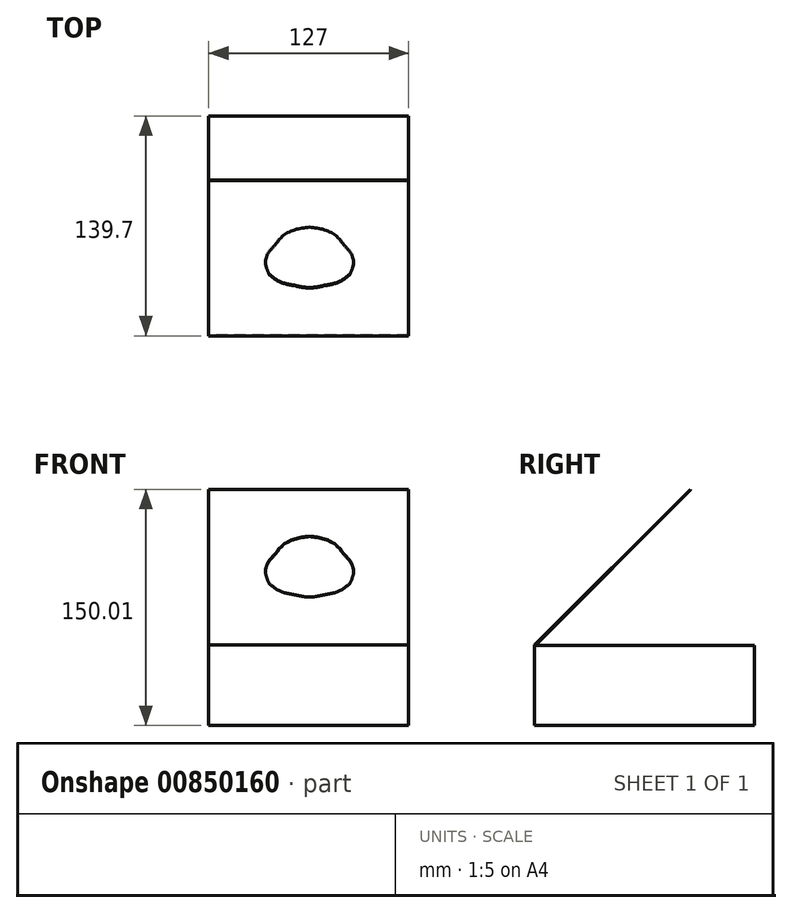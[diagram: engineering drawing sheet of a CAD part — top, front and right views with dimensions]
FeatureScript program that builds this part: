
annotation { "Feature Type Name" : "Feature", "Feature Type Description" : "" }
export const myFeature = defineFeature(function(context is Context, id is Id, definition is map)
    precondition{}
    {
        {
            var Q0;
            Q0=qCreatedBy(makeId("Right.planeOp"),FACE);
            var sketch = newSketch(context, id + "F0", { "sketchPlane" : qUnion([Q0])});
            skLineSegment(sketch, "E0.bottom", {"start": v(0, 0) * mm, "end": v(-139.7, 0) * mm});
            skLineSegment(sketch, "E0.top", {"start": v(0, 50.8) * mm, "end": v(-139.3, 50.8) * mm});
            skLineSegment(sketch, "E0.left", {"start": v(0, 0) * mm, "end": v(0, 50.8) * mm});
            skLineSegment(sketch, "E0.right", {"start": v(-139.7, 0) * mm, "end": v(-139.7, 51.22) * mm});
            skLineSegment(sketch, "E1", {"start": v(-139.7, 51.22) * mm, "end": v(-40.92, 150) * mm});
            skLineSegment(sketch, "E2", {"start": v(-40.92, 150) * mm, "end": v(-40.63, 149.72) * mm});
            skLineSegment(sketch, "E3", {"start": v(-40.63, 149.72) * mm, "end": v(-139.3, 51.05) * mm});
            skLineSegment(sketch, "E4", {"start": v(-139.3, 50.8) * mm, "end": v(-139.3, 51.05) * mm});
            skLineSegment(sketch, "E5", {"start": v(-139.3, 50.8) * mm, "end": v(-139.7, 50.8) * mm, "construction": true});
            skSolve(sketch);
        }
        {
            var Q0;
            Q0=qSketchRegion(id+"F0",true);
            extrude(context, id + "F1", {"entities" : qUnion([Q0]), "endBound" : BoundingType.SYMMETRIC, "depth" : 127 * mm, "offsetDistance" : 25.4 * mm});
        }
        {
            var Q0;
            Q0=makeQuery(id+"F1.opExtrude","SWEPT_FACE",FACE,{"disambiguationData":[OSD([sQuery(id+"F0.wireOp",EDGE,"E1")])]});
            var sketch = newSketch(context, id + "F2", { "sketchPlane" : qUnion([Q0])});
            skLineSegment(sketch, "E6", {"start": v(63.98, -62.06) * mm, "end": v(63.98, 76.85) * mm, "construction": true});
            skLineSegment(sketch, "E7", {"start": v(63.98, -62.06) * mm, "end": v(-63.02, -62.06) * mm, "construction": true});
            skLineSegment(sketch, "E8", {"start": v(-63.02, 76.85) * mm, "end": v(63.98, 76.85) * mm, "construction": true});
            skLineSegment(sketch, "E9", {"start": v(-63.02, -62.06) * mm, "end": v(-63.02, 76.85) * mm, "construction": true});
            skFitSpline(sketch, "E10", {"points": [v(25.88, -7.69) * mm, v(28.32, 1.23) * mm, v(26.98, 11.13) * mm, v(22.26, 19.08) * mm]});
            skFitSpline(sketch, "E11", {"points": [v(22.26, 19.08) * mm, v(17.53, 27.04) * mm, v(9.49, 32.95) * mm, v(0.48, 35.08) * mm]});
            skFitSpline(sketch, "E12", {"points": [v(0.48, 35.08) * mm, v(-8.52, 32.95) * mm, v(-16.57, 27.04) * mm, v(-21.29, 19.08) * mm]});
            skFitSpline(sketch, "E13", {"points": [v(-21.29, 19.08) * mm, v(-26.01, 11.13) * mm, v(-27.35, 1.23) * mm, v(-24.92, -7.69) * mm]});
            skFitSpline(sketch, "E14", {"points": [v(-24.92, -7.69) * mm, v(-20.62, -12.35) * mm, v(-15, -15.78) * mm, v(-8.9, -17.5) * mm]});
            skFitSpline(sketch, "E15", {"points": [v(-8.9, -17.5) * mm, v(-2.8, -19.22) * mm, v(3.77, -19.22) * mm, v(9.87, -17.5) * mm]});
            skFitSpline(sketch, "E16", {"points": [v(9.87, -17.5) * mm, v(15.97, -15.78) * mm, v(21.58, -12.35) * mm, v(25.88, -7.69) * mm]});
            skSolve(sketch);
        }
        {
            var Q0;
            Q0=qSketchRegion(id+"F2",true);
            var Q1;
            Q1=makeQuery(id+"F1.opExtrude","SWEPT_FACE",FACE,{"disambiguationData":[OSD([sQuery(id+"F0.wireOp",EDGE,"E3")])]});
            extrude(context, id + "F3", {"entities" : qUnion([Q0]), "operationType" : NewBodyOperationType.REMOVE, "endBound" : BoundingType.UP_TO_SURFACE, "oppositeDirection" : true, "depth" : 25.4 * mm, "endBoundEntityFace" : qUnion([Q1]), "offsetDistance" : 25.4 * mm});
        }
    });
